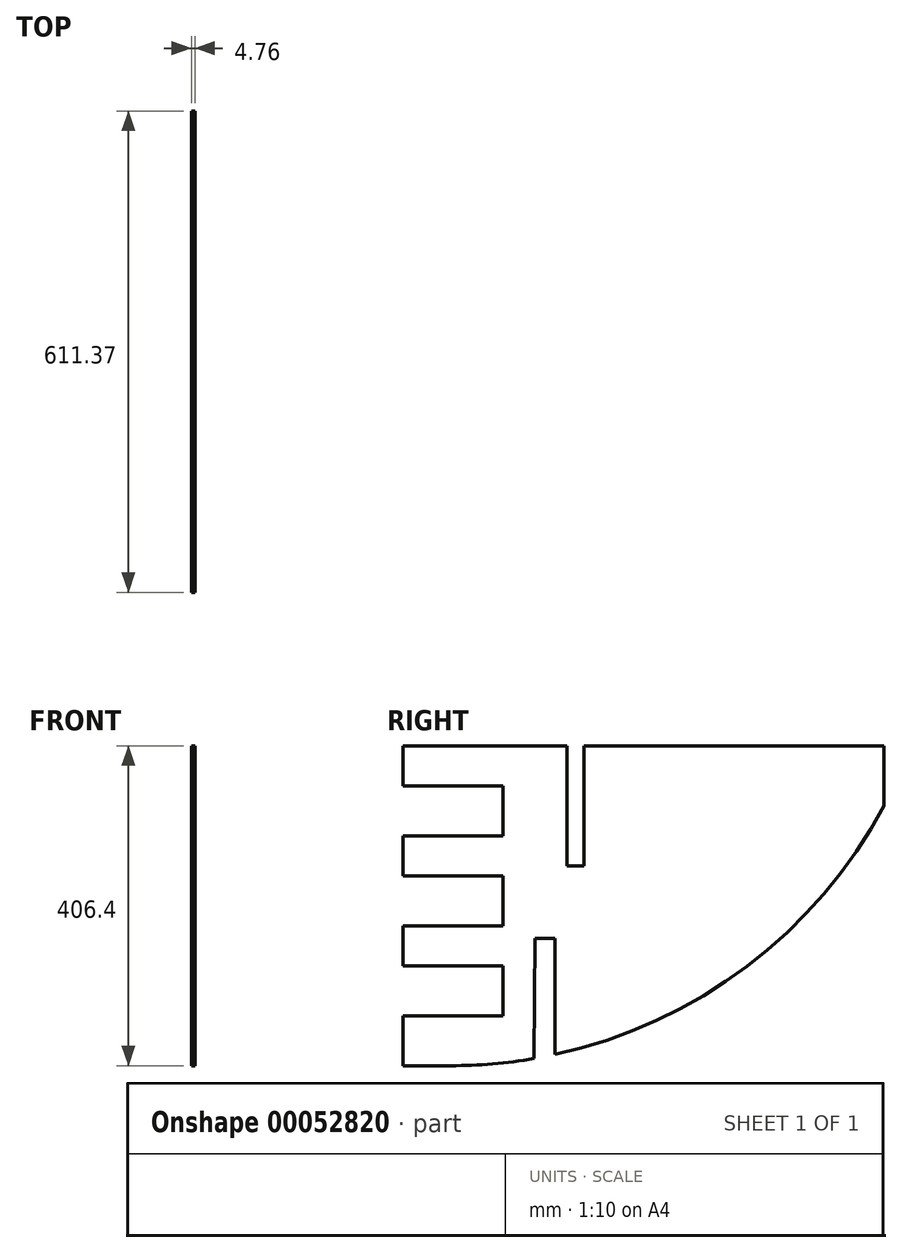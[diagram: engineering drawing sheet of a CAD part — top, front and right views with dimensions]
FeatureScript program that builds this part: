
annotation { "Feature Type Name" : "Feature", "Feature Type Description" : "" }
export const myFeature = defineFeature(function(context is Context, id is Id, definition is map)
    precondition{}
    {
        {
            var Q0;
            Q0=qCreatedBy(makeId("Front.planeOp"),FACE);
            var sketch = newSketch(context, id + "F0", { "sketchPlane" : qUnion([Q0])});
            skLineSegment(sketch, "E0", {"start": v(-611.37, 0) * mm, "end": v(-230.37, 0) * mm});
            skLineSegment(sketch, "E1", {"start": v(0, -406.4) * mm, "end": v(0, -342.9) * mm});
            skLineSegment(sketch, "E2", {"start": v(-611.37, 0) * mm, "end": v(-611.37, -76.2) * mm});
            skLineSegment(sketch, "E3", {"start": v(0, -406.4) * mm, "end": v(-60.96, -406.4) * mm});
            skArc(sketch, "E4", {"start": v(-611.37, -76.2) * mm, "mid": v(-437.22, -280.16) * mm, "end": v(-193.52, -392.15) * mm});
            skLineSegment(sketch, "E5", {"start": v(0, -50.8) * mm, "end": v(-127, -50.8) * mm});
            skLineSegment(sketch, "E6", {"start": v(-127, -50.8) * mm, "end": v(-127, -114.3) * mm});
            skLineSegment(sketch, "E7", {"start": v(-127, -114.3) * mm, "end": v(0, -114.3) * mm});
            skLineSegment(sketch, "E8", {"start": v(0, -165.1) * mm, "end": v(-127, -165.1) * mm});
            skLineSegment(sketch, "E9", {"start": v(-127, -165.1) * mm, "end": v(-127, -228.6) * mm});
            skLineSegment(sketch, "E10", {"start": v(-127, -228.6) * mm, "end": v(0, -228.6) * mm});
            skLineSegment(sketch, "E11", {"start": v(0, -279.4) * mm, "end": v(-127, -279.4) * mm});
            skLineSegment(sketch, "E12", {"start": v(-127, -279.4) * mm, "end": v(-127, -342.9) * mm});
            skLineSegment(sketch, "E13", {"start": v(-127, -342.9) * mm, "end": v(0, -342.9) * mm});
            skLineSegment(sketch, "E14.trimOffspring", {"start": v(0, -50.8) * mm, "end": v(0, 0) * mm});
            skLineSegment(sketch, "E15.trimOffspring", {"start": v(0, -165.1) * mm, "end": v(0, -114.3) * mm});
            skLineSegment(sketch, "E16.trimOffspring", {"start": v(0, -279.4) * mm, "end": v(0, -228.6) * mm});
            skLineSegment(sketch, "E17", {"start": v(-230.37, 0) * mm, "end": v(-230.37, -152.4) * mm});
            skLineSegment(sketch, "E18", {"start": v(-230.37, -152.4) * mm, "end": v(-208.6, -152.4) * mm});
            skLineSegment(sketch, "E19", {"start": v(-208.6, -152.4) * mm, "end": v(-208.6, 0) * mm});
            skLineSegment(sketch, "E20.trimOffspring", {"start": v(-208.6, 0) * mm, "end": v(0, 0) * mm});
            skLineSegment(sketch, "E21", {"start": v(-193.52, -392.15) * mm, "end": v(-193.52, -244.94) * mm});
            skLineSegment(sketch, "E22", {"start": v(-193.52, -244.94) * mm, "end": v(-168.12, -244.94) * mm});
            skLineSegment(sketch, "E23", {"start": v(-168.12, -244.94) * mm, "end": v(-166.92, -397.34) * mm});
            skArc(sketch, "E24.trimOffspring", {"start": v(-166.92, -397.34) * mm, "mid": v(-114.13, -404.13) * mm, "end": v(-60.96, -406.4) * mm});
            skSolve(sketch);
        }
        {
            var Q0;
            Q0=makeQuery(id+"F0.imprint","IMPRINT",FACE,{"disambiguationData":[TD([[makeQuery(id+"F0.imprint","IMPRINT",EDGE,{"derivedFrom":sQuery(id+"F0.wireOp",EDGE,"E0")}),-1.0]])]});
            extrude(context, id + "F1", {"entities" : qUnion([Q0]), "depth" : 4.76 * mm});
        }
        {
            var Q0;
            Q0=makeQuery(id+"F1.opExtrude","SWEPT_BODY",BODY,{"disambiguationData":[OSD([sQuery(id+"F0.wireOp",EDGE,"E0"),sQuery(id+"F0.wireOp",EDGE,"E1"),sQuery(id+"F0.wireOp",EDGE,"E2"),sQuery(id+"F0.wireOp",EDGE,"E3"),sQuery(id+"F0.wireOp",EDGE,"E4"),sQuery(id+"F0.wireOp",EDGE,"E5"),sQuery(id+"F0.wireOp",EDGE,"E6"),sQuery(id+"F0.wireOp",EDGE,"E7"),sQuery(id+"F0.wireOp",EDGE,"E8"),sQuery(id+"F0.wireOp",EDGE,"E9"),sQuery(id+"F0.wireOp",EDGE,"E10"),sQuery(id+"F0.wireOp",EDGE,"E11"),sQuery(id+"F0.wireOp",EDGE,"E12"),sQuery(id+"F0.wireOp",EDGE,"E13"),sQuery(id+"F0.wireOp",EDGE,"E14.trimOffspring"),sQuery(id+"F0.wireOp",EDGE,"E15.trimOffspring"),sQuery(id+"F0.wireOp",EDGE,"E16.trimOffspring"),sQuery(id+"F0.wireOp",EDGE,"E17"),sQuery(id+"F0.wireOp",EDGE,"E18"),sQuery(id+"F0.wireOp",EDGE,"E19"),sQuery(id+"F0.wireOp",EDGE,"E20.trimOffspring"),sQuery(id+"F0.wireOp",EDGE,"E21"),sQuery(id+"F0.wireOp",EDGE,"E22"),sQuery(id+"F0.wireOp",EDGE,"E23")])]});
            var Q1;
            Q1=makeQuery(id+"F1.opExtrude","CAP_EDGE",EDGE,{"disambiguationData":[OSD([sQuery(id+"F0.wireOp",EDGE,"E15.trimOffspring")])],"isStart":true});
            transform(context, id + "F2", {"entities" : qUnion([Q0]), "transformType" : TransformType.ROTATION, "transformAxis" : qUnion([Q1]), "angle" : 270 * degree, "makeCopy" : false});
        }
    });
